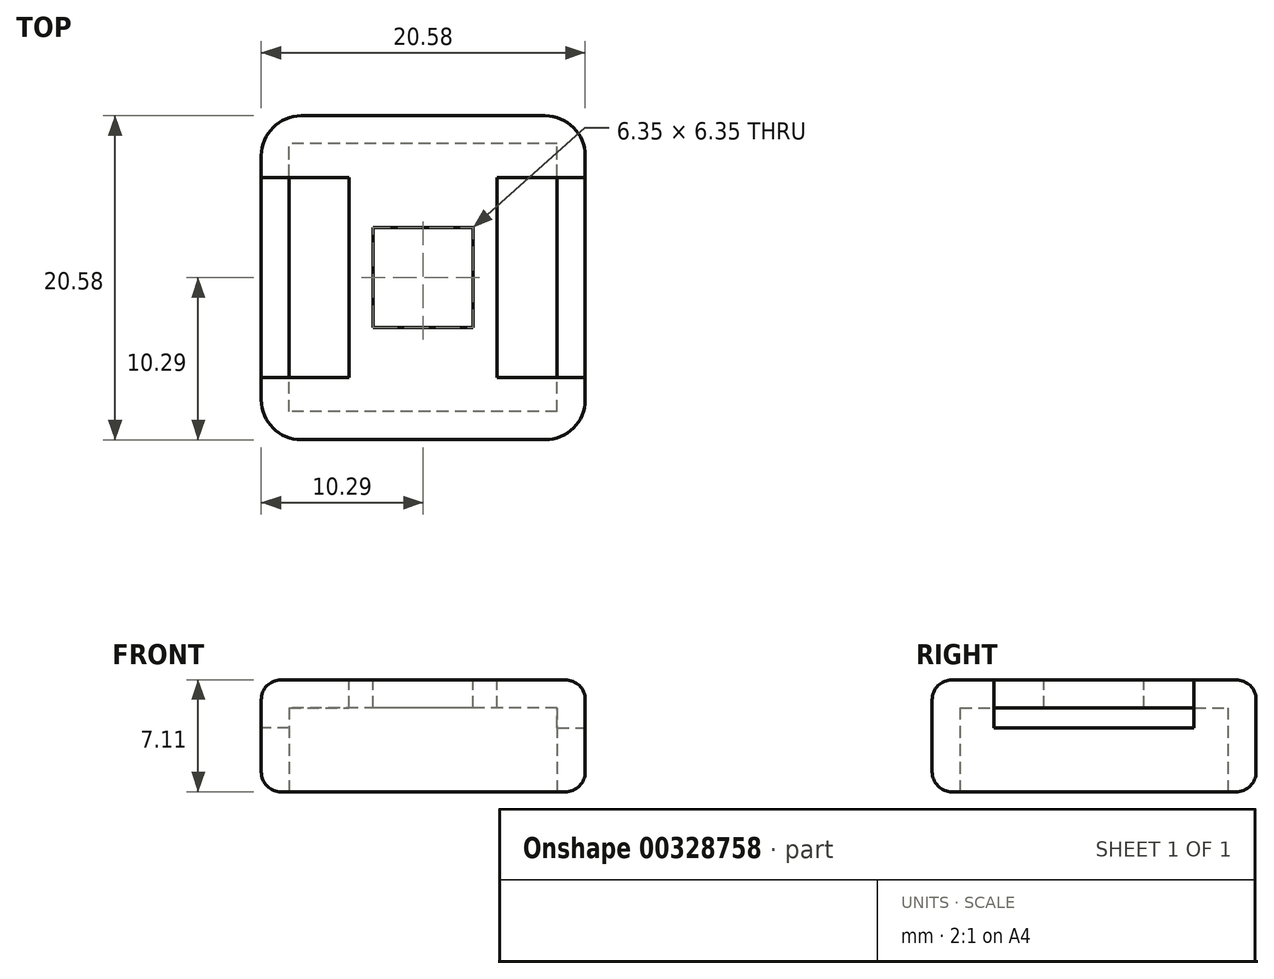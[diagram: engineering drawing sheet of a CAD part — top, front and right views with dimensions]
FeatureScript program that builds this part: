
annotation { "Feature Type Name" : "Feature", "Feature Type Description" : "" }
export const myFeature = defineFeature(function(context is Context, id is Id, definition is map)
    precondition{}
    {
        {
            var Q0;
            Q0=qCreatedBy(makeId("Top.planeOp"),FACE);
            var sketch = newSketch(context, id + "F0", { "sketchPlane" : qUnion([Q0])});
            skLineSegment(sketch, "E0.bottom", {"start": v(10.29, 10.29) * mm, "end": v(-10.29, 10.29) * mm});
            skLineSegment(sketch, "E0.top", {"start": v(10.29, -10.29) * mm, "end": v(-10.29, -10.29) * mm});
            skLineSegment(sketch, "E0.left", {"start": v(10.29, 10.29) * mm, "end": v(10.29, -10.29) * mm});
            skLineSegment(sketch, "E0.right", {"start": v(-10.29, 10.29) * mm, "end": v(-10.29, -10.29) * mm});
            skPoint(sketch, "E0.middle", {"position": v(0, 0) * mm});
            skSolve(sketch);
        }
        {
            var Q0;
            Q0=qSketchRegion(id+"F0",true);
            extrude(context, id + "F1", {"entities" : qUnion([Q0]), "depth" : 7.11 * mm});
        }
        {
            var Q0;
            Q0=makeQuery(id+"F1.opExtrude","CAP_FACE",FACE,{"disambiguationData":[OSD([sQuery(id+"F0.wireOp",EDGE,"E0.bottom"),sQuery(id+"F0.wireOp",EDGE,"E0.top"),sQuery(id+"F0.wireOp",EDGE,"E0.left"),sQuery(id+"F0.wireOp",EDGE,"E0.right")])],"isStart":true});
            var sketch = newSketch(context, id + "F2", { "sketchPlane" : qUnion([Q0])});
            skLineSegment(sketch, "E1.bottom", {"start": v(8.5, 8.5) * mm, "end": v(-8.5, 8.5) * mm});
            skLineSegment(sketch, "E1.top", {"start": v(8.5, -8.5) * mm, "end": v(-8.5, -8.5) * mm});
            skLineSegment(sketch, "E1.left", {"start": v(8.5, 8.5) * mm, "end": v(8.5, -8.5) * mm});
            skLineSegment(sketch, "E1.right", {"start": v(-8.5, 8.5) * mm, "end": v(-8.5, -8.5) * mm});
            skPoint(sketch, "E1.middle", {"position": v(0, 0) * mm});
            skSolve(sketch);
        }
        {
            var Q0;
            Q0=makeQuery(id+"F2.imprint","IMPRINT",FACE,{"disambiguationData":[TD([[makeQuery(id+"F2.imprint","IMPRINT",EDGE,{"derivedFrom":sQuery(id+"F2.wireOp",EDGE,"E1.bottom")}),1.0]])]});
            extrude(context, id + "F3", {"entities" : qUnion([Q0]), "operationType" : NewBodyOperationType.REMOVE, "oppositeDirection" : true, "depth" : 5.33 * mm});
        }
        {
            var Q0;
            Q0=makeQuery(id+"F1.opExtrude","SWEPT_EDGE",EDGE,{"disambiguationData":[OSD([sQuery(id+"F0.wireOp",EDGE,"E0.top"),sQuery(id+"F0.wireOp",EDGE,"E0.right")])]});
            var Q1;
            Q1=makeQuery(id+"F1.opExtrude","SWEPT_EDGE",EDGE,{"disambiguationData":[OSD([sQuery(id+"F0.wireOp",EDGE,"E0.bottom"),sQuery(id+"F0.wireOp",EDGE,"E0.left")])]});
            var Q2;
            Q2=makeQuery(id+"F1.opExtrude","SWEPT_EDGE",EDGE,{"disambiguationData":[OSD([sQuery(id+"F0.wireOp",EDGE,"E0.top"),sQuery(id+"F0.wireOp",EDGE,"E0.left")])]});
            var Q3;
            Q3=makeQuery(id+"F1.opExtrude","SWEPT_EDGE",EDGE,{"disambiguationData":[OSD([sQuery(id+"F0.wireOp",EDGE,"E0.bottom"),sQuery(id+"F0.wireOp",EDGE,"E0.right")])]});
            fillet(context, id + "F4", {"entities" : qUnion([Q0, Q1, Q2, Q3]), "radius" : 2.54 * mm, "tangentPropagation" : true, "allowEdgeOverflow" : false});
        }
        {
            var Q0;
            Q0=makeQuery(id+"F1.opExtrude","CAP_FACE",FACE,{"disambiguationData":[OSD([sQuery(id+"F0.wireOp",EDGE,"E0.bottom"),sQuery(id+"F0.wireOp",EDGE,"E0.top"),sQuery(id+"F0.wireOp",EDGE,"E0.left"),sQuery(id+"F0.wireOp",EDGE,"E0.right")])],"isStart":false});
            var sketch = newSketch(context, id + "F5", { "sketchPlane" : qUnion([Q0])});
            skLineSegment(sketch, "E2.bottom", {"start": v(-4.7, 6.35) * mm, "end": v(-15.88, 6.35) * mm});
            skLineSegment(sketch, "E2.top", {"start": v(-4.7, -6.35) * mm, "end": v(-15.88, -6.35) * mm});
            skLineSegment(sketch, "E2.left", {"start": v(-4.7, 6.35) * mm, "end": v(-4.7, -6.35) * mm});
            skLineSegment(sketch, "E2.right", {"start": v(-15.88, 6.35) * mm, "end": v(-15.88, -6.35) * mm});
            skPoint(sketch, "E2.middle", {"position": v(-10.29, 0) * mm});
            skSolve(sketch);
        }
        {
            var Q0;
            {var subQ0=sQuery(id+"F5.wireOp",EDGE,"E2.left");Q0=makeQuery(id+"F5.imprint","IMPRINT",FACE,{"disambiguationData":[TD([[makeQuery(id+"F5.imprint","IMPRINT",EDGE,{"derivedFrom":subQ0}),-1.0]])]});}
            extrude(context, id + "F6", {"entities" : qUnion([Q0]), "operationType" : NewBodyOperationType.REMOVE, "oppositeDirection" : true, "depth" : 3.05 * mm});
        }
        {
            var Q0;
            Q0=makeQuery(id+"F1.opExtrude","CAP_FACE",FACE,{"disambiguationData":[OSD([sQuery(id+"F0.wireOp",EDGE,"E0.bottom"),sQuery(id+"F0.wireOp",EDGE,"E0.top"),sQuery(id+"F0.wireOp",EDGE,"E0.left"),sQuery(id+"F0.wireOp",EDGE,"E0.right")])],"isStart":false});
            var sketch = newSketch(context, id + "F7", { "sketchPlane" : qUnion([Q0])});
            skLineSegment(sketch, "E3.bottom", {"start": v(4.7, 6.35) * mm, "end": v(15.88, 6.35) * mm});
            skLineSegment(sketch, "E3.top", {"start": v(4.7, -6.35) * mm, "end": v(15.88, -6.35) * mm});
            skLineSegment(sketch, "E3.left", {"start": v(4.7, 6.35) * mm, "end": v(4.7, -6.35) * mm});
            skLineSegment(sketch, "E3.right", {"start": v(15.88, 6.35) * mm, "end": v(15.88, -6.35) * mm});
            skPoint(sketch, "E3.middle", {"position": v(10.29, 0) * mm});
            skSolve(sketch);
        }
        {
            var Q0;
            Q0=qSketchRegion(id+"F7",true);
            extrude(context, id + "F8", {"entities" : qUnion([Q0]), "operationType" : NewBodyOperationType.REMOVE, "oppositeDirection" : true, "depth" : 3.05 * mm});
        }
        {
            var Q0;
            Q0=makeQuery(id+"F1.opExtrude","CAP_FACE",FACE,{"disambiguationData":[OSD([sQuery(id+"F0.wireOp",EDGE,"E0.bottom"),sQuery(id+"F0.wireOp",EDGE,"E0.top"),sQuery(id+"F0.wireOp",EDGE,"E0.left"),sQuery(id+"F0.wireOp",EDGE,"E0.right")])],"isStart":false});
            var sketch = newSketch(context, id + "F9", { "sketchPlane" : qUnion([Q0])});
            skPoint(sketch, "E4.middle", {"position": v(0, 0) * mm});
            skLineSegment(sketch, "E5.bottom", {"start": v(3.18, 3.18) * mm, "end": v(-3.18, 3.18) * mm});
            skLineSegment(sketch, "E5.top", {"start": v(3.17, -3.18) * mm, "end": v(-3.18, -3.18) * mm});
            skLineSegment(sketch, "E5.left", {"start": v(3.18, 3.17) * mm, "end": v(3.17, -3.18) * mm});
            skLineSegment(sketch, "E5.right", {"start": v(-3.18, 3.18) * mm, "end": v(-3.18, -3.17) * mm});
            skSolve(sketch);
        }
        {
            var Q0;
            Q0=qSketchRegion(id+"F9",true);
            extrude(context, id + "F10", {"entities" : qUnion([Q0]), "operationType" : NewBodyOperationType.REMOVE, "oppositeDirection" : true, "depth" : 1.78 * mm});
        }
        {
            var Q0;
            Q0=makeQuery(id+"F1.opExtrude","CAP_EDGE",EDGE,{"disambiguationData":[OSD([sQuery(id+"F0.wireOp",EDGE,"E0.bottom")])],"isStart":false});
            var Q1;
            Q1=makeQuery(id+"F1.opExtrude","CAP_EDGE",EDGE,{"disambiguationData":[OSD([sQuery(id+"F0.wireOp",EDGE,"E0.top")])],"isStart":false});
            fillet(context, id + "F11", {"entities" : qUnion([Q0, Q1]), "radius" : 1.27 * mm, "tangentPropagation" : true, "allowEdgeOverflow" : false});
        }
        {
            var Q0;
            Q0=makeQuery(id+"F1.opExtrude","CAP_EDGE",EDGE,{"disambiguationData":[OSD([sQuery(id+"F0.wireOp",EDGE,"E0.right")])],"isStart":true});
            var Q1;
            Q1=makeQuery(id+"F1.opExtrude","CAP_EDGE",EDGE,{"disambiguationData":[OSD([sQuery(id+"F0.wireOp",EDGE,"E0.bottom")])],"isStart":true});
            var Q2;
            {var subQ0=sQuery(id+"F0.wireOp",EDGE,"E0.right");var subQ1=sQuery(id+"F0.wireOp",EDGE,"E0.bottom");Q2=makeQuery(id+"F4.opFillet","BLEND_EDGE",EDGE,{"blendedFrom":[makeQuery(id+"F1.opExtrude","SWEPT_EDGE",EDGE,{"disambiguationData":[OSD([subQ1,subQ0])]}),makeQuery(id+"F1.opExtrude","CAP_FACE",FACE,{"disambiguationData":[OSD([subQ1,sQuery(id+"F0.wireOp",EDGE,"E0.top"),sQuery(id+"F0.wireOp",EDGE,"E0.left"),subQ0])],"isStart":true})],"blendedInto":[makeQuery(id+"F1.opExtrude","CAP_FACE",FACE,{"disambiguationData":[OSD([subQ1,sQuery(id+"F0.wireOp",EDGE,"E0.top"),sQuery(id+"F0.wireOp",EDGE,"E0.left"),subQ0])],"isStart":true})]});}
            fillet(context, id + "F12", {"entities" : qUnion([Q0, Q1, Q2]), "radius" : 1.27 * mm, "tangentPropagation" : true, "allowEdgeOverflow" : false});
        }
    });
